# Revit family: Data_Device-Work_Area-Leviton-Surface-Mount-Housing
name_source: partatom
category: Data Devices
units: mm (PartAtom-declared; Revit-internal decimal feet)

## family parameters
Cut with Voids When Loaded = No
Host = Face
Maintain Annotation Orientation = Yes
OmniClass Number = 23.85.50.21
OmniClass Title = Cable Transmission and Reception Equipment
Part Type = Normal
Room Calculation Point = No
Round Connector Dimension = Use Diameter
Shared = Yes

## types (7) — shared parameters
Annotation Symbol is Visible = Yes
Assembly Code = D5030600
Check for Latest Version = http://www.leviton.com
Date Last Modified = January 1, 2017
Default Elevation = 18 "
Description = Surface-Mount QuickPort Box
Equipment Abbreviation = QPSM
Family Version = 1.0.0
Manufacturer = Leviton
Model Disclaimer = http://www.leviton.com
Part Description = Surface-Mount QuickPort Box
Product Documentation Link = http://www.leviton.com
URL = http://www.leviton.com
z Collapse = Yes
zero-valued in all types: Minimum Order Quantity, Quantity per Package, z Distance

## per-type parameters (varying)
| type | Plenum Rated | Shielded | z Depth | z Has 01 Port | z Has 02 Ports | z Has 02 S Ports | z Has 04 Ports | z Has 04 S Ports | z Has 06 Ports | z Has 12 Ports | z Leviton Type | z Width |
| 4-Port | No | No | 1.05 " | No | No | No | Yes | No | No | No | 4 | 3.22 " |
| 6-Port | No | No | 1.09 " | No | No | No | No | No | Yes | No | 6 | 3.25 " |
| 2-Port | Yes | No | 1.1 " | No | Yes | No | No | No | No | No | 2 | 2.25 " |
| 1-Port | Yes | No | 1.01 " | Yes | No | No | No | No | No | No | 1 | 2.28 " |
| 12-Port | No | No | 1.12 " | No | No | No | No | No | No | Yes | 12 | 5.04 " |
| 4-Port, Shielded | No | Yes | 1.22 " | No | No | No | No | Yes | No | No | 5 | 5.2 " |
| 2-Port, Shielded | No | Yes | 1.22 " | No | No | Yes | No | No | No | No | 3 | 3 " |

## geometry (parser evidence)
native form markers: Blend x38, Sweep x5
no freeform markers — native parametric forms only
